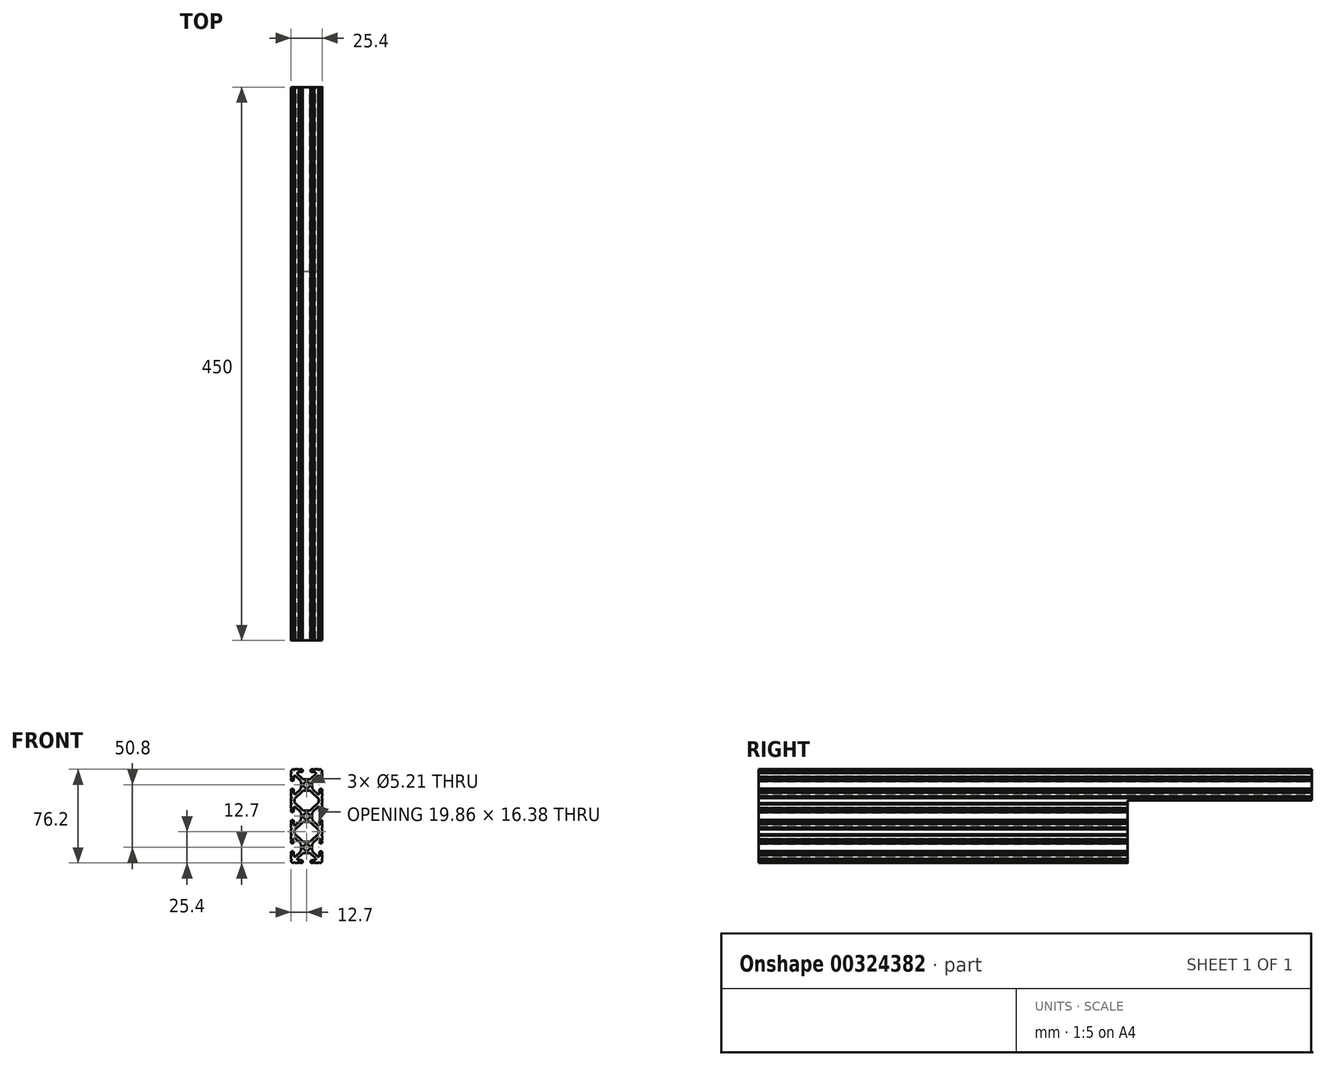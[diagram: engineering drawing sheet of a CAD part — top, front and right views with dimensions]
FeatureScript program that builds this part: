
annotation { "Feature Type Name" : "Feature", "Feature Type Description" : "" }
export const myFeature = defineFeature(function(context is Context, id is Id, definition is map)
    precondition{}
    {
        {
            var Q0;
            Q0=qCreatedBy(makeId("Front.planeOp"),FACE);
            var sketch = newSketch(context, id + "F0", { "sketchPlane" : qUnion([Q0])});
            skArc(sketch, "E0", {"start": v(2.6, 25.4) * mm, "mid": v(0, 28) * mm, "end": v(-2.6, 25.4) * mm});
            skArc(sketch, "E1", {"start": v(-2.6, 25.4) * mm, "mid": v(0, 22.8) * mm, "end": v(2.6, 25.4) * mm});
            skArc(sketch, "E2", {"start": v(-10.57, 38.1) * mm, "mid": v(-10.06, 37.6) * mm, "end": v(-9.55, 38.1) * mm});
            skArc(sketch, "E3", {"start": v(-10.57, 38.1) * mm, "mid": v(-12.08, 37.48) * mm, "end": v(-12.7, 35.97) * mm});
            skArc(sketch, "E4", {"start": v(-12.7, 34.95) * mm, "mid": v(-12.2, 35.46) * mm, "end": v(-12.7, 35.97) * mm});
            skLineSegment(sketch, "E5", {"start": v(-12.7, 34.95) * mm, "end": v(-12.7, 31.72) * mm});
            skArc(sketch, "E6", {"start": v(-12.7, 30.7) * mm, "mid": v(-12.2, 31.22) * mm, "end": v(-12.7, 31.72) * mm});
            skLineSegment(sketch, "E7", {"start": v(-12.7, 30.7) * mm, "end": v(-12.7, 29.7) * mm});
            skArc(sketch, "E8", {"start": v(-12.7, 29.7) * mm, "mid": v(-11.6, 28.6) * mm, "end": v(-10.5, 29.7) * mm});
            skLineSegment(sketch, "E9", {"start": v(-10.5, 29.7) * mm, "end": v(-10.5, 31.87) * mm});
            skArc(sketch, "E10", {"start": v(-8.76, 32.6) * mm, "mid": v(-9.86, 32.81) * mm, "end": v(-10.5, 31.87) * mm});
            skLineSegment(sketch, "E11", {"start": v(-8.76, 32.6) * mm, "end": v(-5.44, 29.28) * mm});
            skArc(sketch, "E12", {"start": v(-4.5, 27.03) * mm, "mid": v(-4.75, 28.25) * mm, "end": v(-5.44, 29.28) * mm});
            skLineSegment(sketch, "E13", {"start": v(-4.5, 27.03) * mm, "end": v(-4.5, 23.77) * mm});
            skArc(sketch, "E14", {"start": v(-5.44, 21.52) * mm, "mid": v(-4.75, 22.55) * mm, "end": v(-4.5, 23.77) * mm});
            skLineSegment(sketch, "E15", {"start": v(-5.44, 21.52) * mm, "end": v(-8.76, 18.2) * mm});
            skArc(sketch, "E16", {"start": v(-10.5, 18.93) * mm, "mid": v(-9.86, 17.99) * mm, "end": v(-8.76, 18.2) * mm});
            skLineSegment(sketch, "E17", {"start": v(-10.5, 18.93) * mm, "end": v(-10.5, 21.1) * mm});
            skArc(sketch, "E18", {"start": v(-10.5, 21.1) * mm, "mid": v(-11.6, 22.2) * mm, "end": v(-12.7, 21.1) * mm});
            skLineSegment(sketch, "E19", {"start": v(-12.7, 21.1) * mm, "end": v(-12.7, 20.1) * mm});
            skArc(sketch, "E20", {"start": v(-12.7, 19.08) * mm, "mid": v(-12.2, 19.58) * mm, "end": v(-12.7, 20.1) * mm});
            skLineSegment(sketch, "E21", {"start": v(-12.7, 19.08) * mm, "end": v(-12.7, 15.85) * mm});
            skArc(sketch, "E22", {"start": v(-12.7, 14.83) * mm, "mid": v(-12.2, 15.34) * mm, "end": v(-12.7, 15.85) * mm});
            skLineSegment(sketch, "E23", {"start": v(-12.7, 14.83) * mm, "end": v(-12.7, 10.57) * mm});
            skArc(sketch, "E24", {"start": v(-12.7, 9.55) * mm, "mid": v(-12.2, 10.06) * mm, "end": v(-12.7, 10.57) * mm});
            skLineSegment(sketch, "E25", {"start": v(-12.7, 9.55) * mm, "end": v(-12.7, 6.32) * mm});
            skArc(sketch, "E26", {"start": v(-12.7, 5.3) * mm, "mid": v(-12.2, 5.82) * mm, "end": v(-12.7, 6.32) * mm});
            skLineSegment(sketch, "E27", {"start": v(-12.7, 5.3) * mm, "end": v(-12.7, 4.3) * mm});
            skArc(sketch, "E28", {"start": v(-12.7, 4.3) * mm, "mid": v(-11.6, 3.2) * mm, "end": v(-10.5, 4.3) * mm});
            skLineSegment(sketch, "E29", {"start": v(-10.5, 4.3) * mm, "end": v(-10.5, 6.47) * mm});
            skArc(sketch, "E30", {"start": v(-8.76, 7.2) * mm, "mid": v(-9.86, 7.41) * mm, "end": v(-10.5, 6.47) * mm});
            skLineSegment(sketch, "E31", {"start": v(-8.76, 7.2) * mm, "end": v(-5.44, 3.88) * mm});
            skArc(sketch, "E32", {"start": v(-4.5, 1.63) * mm, "mid": v(-4.75, 2.85) * mm, "end": v(-5.44, 3.88) * mm});
            skLineSegment(sketch, "E33", {"start": v(-4.5, 1.63) * mm, "end": v(-4.5, -1.63) * mm});
            skArc(sketch, "E34", {"start": v(-5.44, -3.88) * mm, "mid": v(-4.75, -2.85) * mm, "end": v(-4.5, -1.63) * mm});
            skLineSegment(sketch, "E35", {"start": v(-5.44, -3.88) * mm, "end": v(-8.76, -7.2) * mm});
            skArc(sketch, "E36", {"start": v(-10.5, -6.47) * mm, "mid": v(-9.86, -7.41) * mm, "end": v(-8.76, -7.2) * mm});
            skLineSegment(sketch, "E37", {"start": v(-10.5, -6.47) * mm, "end": v(-10.5, -4.3) * mm});
            skArc(sketch, "E38", {"start": v(-10.5, -4.3) * mm, "mid": v(-11.6, -3.2) * mm, "end": v(-12.7, -4.3) * mm});
            skLineSegment(sketch, "E39", {"start": v(-12.7, -4.3) * mm, "end": v(-12.7, -5.3) * mm});
            skArc(sketch, "E40", {"start": v(-12.7, -6.32) * mm, "mid": v(-12.2, -5.82) * mm, "end": v(-12.7, -5.3) * mm});
            skLineSegment(sketch, "E41", {"start": v(-12.7, -6.32) * mm, "end": v(-12.7, -9.55) * mm});
            skArc(sketch, "E42", {"start": v(-12.7, -10.57) * mm, "mid": v(-12.2, -10.06) * mm, "end": v(-12.7, -9.55) * mm});
            skLineSegment(sketch, "E43", {"start": v(-12.7, -10.57) * mm, "end": v(-12.7, -14.83) * mm});
            skArc(sketch, "E44", {"start": v(-12.7, -15.85) * mm, "mid": v(-12.2, -15.34) * mm, "end": v(-12.7, -14.83) * mm});
            skLineSegment(sketch, "E45", {"start": v(-12.7, -15.85) * mm, "end": v(-12.7, -19.08) * mm});
            skArc(sketch, "E46", {"start": v(-12.7, -20.1) * mm, "mid": v(-12.2, -19.58) * mm, "end": v(-12.7, -19.08) * mm});
            skLineSegment(sketch, "E47", {"start": v(-12.7, -20.1) * mm, "end": v(-12.7, -21.1) * mm});
            skArc(sketch, "E48", {"start": v(-12.7, -21.1) * mm, "mid": v(-11.6, -22.2) * mm, "end": v(-10.5, -21.1) * mm});
            skLineSegment(sketch, "E49", {"start": v(-10.5, -21.1) * mm, "end": v(-10.5, -18.93) * mm});
            skArc(sketch, "E50", {"start": v(-8.76, -18.2) * mm, "mid": v(-9.86, -17.99) * mm, "end": v(-10.5, -18.93) * mm});
            skLineSegment(sketch, "E51", {"start": v(-8.76, -18.2) * mm, "end": v(-5.44, -21.52) * mm});
            skArc(sketch, "E52", {"start": v(-4.5, -23.77) * mm, "mid": v(-4.75, -22.55) * mm, "end": v(-5.44, -21.52) * mm});
            skLineSegment(sketch, "E53", {"start": v(-4.5, -23.77) * mm, "end": v(-4.5, -27.03) * mm});
            skArc(sketch, "E54", {"start": v(-5.44, -29.28) * mm, "mid": v(-4.75, -28.25) * mm, "end": v(-4.5, -27.03) * mm});
            skLineSegment(sketch, "E55", {"start": v(-5.44, -29.28) * mm, "end": v(-8.76, -32.6) * mm});
            skArc(sketch, "E56", {"start": v(-10.5, -31.87) * mm, "mid": v(-9.86, -32.81) * mm, "end": v(-8.76, -32.6) * mm});
            skLineSegment(sketch, "E57", {"start": v(-10.5, -31.87) * mm, "end": v(-10.5, -29.7) * mm});
            skArc(sketch, "E58", {"start": v(-10.5, -29.7) * mm, "mid": v(-11.6, -28.6) * mm, "end": v(-12.7, -29.7) * mm});
            skLineSegment(sketch, "E59", {"start": v(-12.7, -29.7) * mm, "end": v(-12.7, -30.7) * mm});
            skArc(sketch, "E60", {"start": v(-12.7, -31.72) * mm, "mid": v(-12.2, -31.22) * mm, "end": v(-12.7, -30.7) * mm});
            skLineSegment(sketch, "E61", {"start": v(-12.7, -31.72) * mm, "end": v(-12.7, -34.95) * mm});
            skArc(sketch, "E62", {"start": v(-12.7, -35.97) * mm, "mid": v(-12.2, -35.46) * mm, "end": v(-12.7, -34.95) * mm});
            skArc(sketch, "E63", {"start": v(-12.7, -35.97) * mm, "mid": v(-12.08, -37.48) * mm, "end": v(-10.57, -38.1) * mm});
            skArc(sketch, "E64", {"start": v(-9.55, -38.1) * mm, "mid": v(-10.06, -37.6) * mm, "end": v(-10.57, -38.1) * mm});
            skLineSegment(sketch, "E65", {"start": v(-9.55, -38.1) * mm, "end": v(-6.32, -38.1) * mm});
            skArc(sketch, "E66", {"start": v(-5.3, -38.1) * mm, "mid": v(-5.82, -37.6) * mm, "end": v(-6.32, -38.1) * mm});
            skLineSegment(sketch, "E67", {"start": v(-5.3, -38.1) * mm, "end": v(-4.3, -38.1) * mm});
            skArc(sketch, "E68", {"start": v(-4.3, -38.1) * mm, "mid": v(-3.2, -37) * mm, "end": v(-4.3, -35.9) * mm});
            skLineSegment(sketch, "E69", {"start": v(-4.3, -35.9) * mm, "end": v(-6.47, -35.9) * mm});
            skArc(sketch, "E70", {"start": v(-7.2, -34.16) * mm, "mid": v(-7.41, -35.26) * mm, "end": v(-6.47, -35.9) * mm});
            skLineSegment(sketch, "E71", {"start": v(-7.2, -34.16) * mm, "end": v(-3.88, -30.84) * mm});
            skArc(sketch, "E72", {"start": v(-1.63, -29.9) * mm, "mid": v(-2.85, -30.15) * mm, "end": v(-3.88, -30.84) * mm});
            skLineSegment(sketch, "E73", {"start": v(-1.63, -29.9) * mm, "end": v(1.63, -29.9) * mm});
            skArc(sketch, "E74", {"start": v(3.88, -30.84) * mm, "mid": v(2.85, -30.15) * mm, "end": v(1.63, -29.9) * mm});
            skLineSegment(sketch, "E75", {"start": v(3.88, -30.84) * mm, "end": v(7.2, -34.16) * mm});
            skArc(sketch, "E76", {"start": v(6.47, -35.9) * mm, "mid": v(7.41, -35.26) * mm, "end": v(7.2, -34.16) * mm});
            skLineSegment(sketch, "E77", {"start": v(6.47, -35.9) * mm, "end": v(4.3, -35.9) * mm});
            skArc(sketch, "E78", {"start": v(4.3, -35.9) * mm, "mid": v(3.2, -37) * mm, "end": v(4.3, -38.1) * mm});
            skLineSegment(sketch, "E79", {"start": v(4.3, -38.1) * mm, "end": v(5.3, -38.1) * mm});
            skArc(sketch, "E80", {"start": v(6.32, -38.1) * mm, "mid": v(5.82, -37.6) * mm, "end": v(5.3, -38.1) * mm});
            skLineSegment(sketch, "E81", {"start": v(6.32, -38.1) * mm, "end": v(9.55, -38.1) * mm});
            skArc(sketch, "E82", {"start": v(10.57, -38.1) * mm, "mid": v(10.06, -37.6) * mm, "end": v(9.55, -38.1) * mm});
            skArc(sketch, "E83", {"start": v(10.57, -38.1) * mm, "mid": v(12.08, -37.48) * mm, "end": v(12.7, -35.97) * mm});
            skArc(sketch, "E84", {"start": v(12.7, -34.95) * mm, "mid": v(12.2, -35.46) * mm, "end": v(12.7, -35.97) * mm});
            skLineSegment(sketch, "E85", {"start": v(12.7, -34.95) * mm, "end": v(12.7, -31.72) * mm});
            skArc(sketch, "E86", {"start": v(12.7, -30.7) * mm, "mid": v(12.2, -31.22) * mm, "end": v(12.7, -31.72) * mm});
            skLineSegment(sketch, "E87", {"start": v(12.7, -30.7) * mm, "end": v(12.7, -29.7) * mm});
            skArc(sketch, "E88", {"start": v(12.7, -29.7) * mm, "mid": v(11.6, -28.6) * mm, "end": v(10.5, -29.7) * mm});
            skLineSegment(sketch, "E89", {"start": v(10.5, -29.7) * mm, "end": v(10.5, -31.87) * mm});
            skArc(sketch, "E90", {"start": v(8.76, -32.6) * mm, "mid": v(9.86, -32.81) * mm, "end": v(10.5, -31.87) * mm});
            skLineSegment(sketch, "E91", {"start": v(8.76, -32.6) * mm, "end": v(5.44, -29.28) * mm});
            skArc(sketch, "E92", {"start": v(4.5, -27.03) * mm, "mid": v(4.75, -28.25) * mm, "end": v(5.44, -29.28) * mm});
            skLineSegment(sketch, "E93", {"start": v(4.5, -27.03) * mm, "end": v(4.5, -23.77) * mm});
            skArc(sketch, "E94", {"start": v(5.44, -21.52) * mm, "mid": v(4.75, -22.55) * mm, "end": v(4.5, -23.77) * mm});
            skLineSegment(sketch, "E95", {"start": v(5.44, -21.52) * mm, "end": v(8.76, -18.2) * mm});
            skArc(sketch, "E96", {"start": v(10.5, -18.93) * mm, "mid": v(9.86, -17.99) * mm, "end": v(8.76, -18.2) * mm});
            skLineSegment(sketch, "E97", {"start": v(10.5, -18.93) * mm, "end": v(10.5, -21.1) * mm});
            skArc(sketch, "E98", {"start": v(10.5, -21.1) * mm, "mid": v(11.6, -22.2) * mm, "end": v(12.7, -21.1) * mm});
            skLineSegment(sketch, "E99", {"start": v(12.7, -21.1) * mm, "end": v(12.7, -20.1) * mm});
            skArc(sketch, "E100", {"start": v(12.7, -19.08) * mm, "mid": v(12.2, -19.58) * mm, "end": v(12.7, -20.1) * mm});
            skLineSegment(sketch, "E101", {"start": v(12.7, -19.08) * mm, "end": v(12.7, -15.85) * mm});
            skArc(sketch, "E102", {"start": v(12.7, -14.83) * mm, "mid": v(12.2, -15.34) * mm, "end": v(12.7, -15.85) * mm});
            skLineSegment(sketch, "E103", {"start": v(12.7, -14.83) * mm, "end": v(12.7, -10.57) * mm});
            skArc(sketch, "E104", {"start": v(12.7, -9.55) * mm, "mid": v(12.2, -10.06) * mm, "end": v(12.7, -10.57) * mm});
            skLineSegment(sketch, "E105", {"start": v(12.7, -9.55) * mm, "end": v(12.7, -6.32) * mm});
            skArc(sketch, "E106", {"start": v(12.7, -5.3) * mm, "mid": v(12.2, -5.82) * mm, "end": v(12.7, -6.32) * mm});
            skLineSegment(sketch, "E107", {"start": v(12.7, -5.3) * mm, "end": v(12.7, -4.3) * mm});
            skArc(sketch, "E108", {"start": v(12.7, -4.3) * mm, "mid": v(11.6, -3.2) * mm, "end": v(10.5, -4.3) * mm});
            skLineSegment(sketch, "E109", {"start": v(10.5, -4.3) * mm, "end": v(10.5, -6.47) * mm});
            skArc(sketch, "E110", {"start": v(8.76, -7.2) * mm, "mid": v(9.86, -7.41) * mm, "end": v(10.5, -6.47) * mm});
            skLineSegment(sketch, "E111", {"start": v(8.76, -7.2) * mm, "end": v(5.44, -3.88) * mm});
            skArc(sketch, "E112", {"start": v(4.5, -1.63) * mm, "mid": v(4.75, -2.85) * mm, "end": v(5.44, -3.88) * mm});
            skLineSegment(sketch, "E113", {"start": v(4.5, -1.63) * mm, "end": v(4.5, 1.63) * mm});
            skArc(sketch, "E114", {"start": v(5.44, 3.88) * mm, "mid": v(4.75, 2.85) * mm, "end": v(4.5, 1.63) * mm});
            skLineSegment(sketch, "E115", {"start": v(5.44, 3.88) * mm, "end": v(8.76, 7.2) * mm});
            skArc(sketch, "E116", {"start": v(10.5, 6.47) * mm, "mid": v(9.86, 7.41) * mm, "end": v(8.76, 7.2) * mm});
            skLineSegment(sketch, "E117", {"start": v(10.5, 6.47) * mm, "end": v(10.5, 4.3) * mm});
            skArc(sketch, "E118", {"start": v(10.5, 4.3) * mm, "mid": v(11.6, 3.2) * mm, "end": v(12.7, 4.3) * mm});
            skLineSegment(sketch, "E119", {"start": v(12.7, 4.3) * mm, "end": v(12.7, 5.3) * mm});
            skArc(sketch, "E120", {"start": v(12.7, 6.32) * mm, "mid": v(12.2, 5.82) * mm, "end": v(12.7, 5.3) * mm});
            skLineSegment(sketch, "E121", {"start": v(12.7, 6.32) * mm, "end": v(12.7, 9.55) * mm});
            skArc(sketch, "E122", {"start": v(12.7, 10.57) * mm, "mid": v(12.2, 10.06) * mm, "end": v(12.7, 9.55) * mm});
            skLineSegment(sketch, "E123", {"start": v(12.7, 10.57) * mm, "end": v(12.7, 14.83) * mm});
            skArc(sketch, "E124", {"start": v(12.7, 15.85) * mm, "mid": v(12.2, 15.34) * mm, "end": v(12.7, 14.83) * mm});
            skLineSegment(sketch, "E125", {"start": v(12.7, 15.85) * mm, "end": v(12.7, 19.08) * mm});
            skArc(sketch, "E126", {"start": v(12.7, 20.1) * mm, "mid": v(12.2, 19.58) * mm, "end": v(12.7, 19.08) * mm});
            skLineSegment(sketch, "E127", {"start": v(12.7, 20.1) * mm, "end": v(12.7, 21.1) * mm});
            skArc(sketch, "E128", {"start": v(12.7, 21.1) * mm, "mid": v(11.6, 22.2) * mm, "end": v(10.5, 21.1) * mm});
            skLineSegment(sketch, "E129", {"start": v(10.5, 21.1) * mm, "end": v(10.5, 18.93) * mm});
            skArc(sketch, "E130", {"start": v(8.76, 18.2) * mm, "mid": v(9.86, 17.99) * mm, "end": v(10.5, 18.93) * mm});
            skLineSegment(sketch, "E131", {"start": v(8.76, 18.2) * mm, "end": v(5.44, 21.52) * mm});
            skArc(sketch, "E132", {"start": v(4.5, 23.77) * mm, "mid": v(4.75, 22.55) * mm, "end": v(5.44, 21.52) * mm});
            skLineSegment(sketch, "E133", {"start": v(4.5, 23.77) * mm, "end": v(4.5, 27.03) * mm});
            skArc(sketch, "E134", {"start": v(5.44, 29.28) * mm, "mid": v(4.75, 28.25) * mm, "end": v(4.5, 27.03) * mm});
            skLineSegment(sketch, "E135", {"start": v(5.44, 29.28) * mm, "end": v(8.76, 32.6) * mm});
            skArc(sketch, "E136", {"start": v(10.5, 31.87) * mm, "mid": v(9.86, 32.81) * mm, "end": v(8.76, 32.6) * mm});
            skLineSegment(sketch, "E137", {"start": v(10.5, 31.87) * mm, "end": v(10.5, 29.7) * mm});
            skArc(sketch, "E138", {"start": v(10.5, 29.7) * mm, "mid": v(11.6, 28.6) * mm, "end": v(12.7, 29.7) * mm});
            skLineSegment(sketch, "E139", {"start": v(12.7, 29.7) * mm, "end": v(12.7, 30.7) * mm});
            skArc(sketch, "E140", {"start": v(12.7, 31.72) * mm, "mid": v(12.2, 31.22) * mm, "end": v(12.7, 30.7) * mm});
            skLineSegment(sketch, "E141", {"start": v(12.7, 31.72) * mm, "end": v(12.7, 34.95) * mm});
            skArc(sketch, "E142", {"start": v(12.7, 35.97) * mm, "mid": v(12.2, 35.46) * mm, "end": v(12.7, 34.95) * mm});
            skArc(sketch, "E143", {"start": v(12.7, 35.97) * mm, "mid": v(12.08, 37.48) * mm, "end": v(10.57, 38.1) * mm});
            skArc(sketch, "E144", {"start": v(9.55, 38.1) * mm, "mid": v(10.06, 37.6) * mm, "end": v(10.57, 38.1) * mm});
            skLineSegment(sketch, "E145", {"start": v(9.55, 38.1) * mm, "end": v(6.32, 38.1) * mm});
            skArc(sketch, "E146", {"start": v(5.3, 38.1) * mm, "mid": v(5.82, 37.6) * mm, "end": v(6.32, 38.1) * mm});
            skLineSegment(sketch, "E147", {"start": v(5.3, 38.1) * mm, "end": v(4.3, 38.1) * mm});
            skArc(sketch, "E148", {"start": v(4.3, 38.1) * mm, "mid": v(3.2, 37) * mm, "end": v(4.3, 35.9) * mm});
            skLineSegment(sketch, "E149", {"start": v(4.3, 35.9) * mm, "end": v(6.47, 35.9) * mm});
            skArc(sketch, "E150", {"start": v(7.2, 34.16) * mm, "mid": v(7.41, 35.26) * mm, "end": v(6.47, 35.9) * mm});
            skLineSegment(sketch, "E151", {"start": v(7.2, 34.16) * mm, "end": v(3.88, 30.84) * mm});
            skArc(sketch, "E152", {"start": v(1.63, 29.9) * mm, "mid": v(2.85, 30.15) * mm, "end": v(3.88, 30.84) * mm});
            skLineSegment(sketch, "E153", {"start": v(1.63, 29.9) * mm, "end": v(-1.63, 29.9) * mm});
            skArc(sketch, "E154", {"start": v(-3.88, 30.84) * mm, "mid": v(-2.85, 30.15) * mm, "end": v(-1.63, 29.9) * mm});
            skLineSegment(sketch, "E155", {"start": v(-3.88, 30.84) * mm, "end": v(-7.2, 34.16) * mm});
            skArc(sketch, "E156", {"start": v(-6.47, 35.9) * mm, "mid": v(-7.41, 35.26) * mm, "end": v(-7.2, 34.16) * mm});
            skLineSegment(sketch, "E157", {"start": v(-6.47, 35.9) * mm, "end": v(-4.3, 35.9) * mm});
            skArc(sketch, "E158", {"start": v(-4.3, 35.9) * mm, "mid": v(-3.2, 37) * mm, "end": v(-4.3, 38.1) * mm});
            skLineSegment(sketch, "E159", {"start": v(-4.3, 38.1) * mm, "end": v(-5.3, 38.1) * mm});
            skArc(sketch, "E160", {"start": v(-6.32, 38.1) * mm, "mid": v(-5.82, 37.6) * mm, "end": v(-5.3, 38.1) * mm});
            skLineSegment(sketch, "E161", {"start": v(-6.32, 38.1) * mm, "end": v(-9.55, 38.1) * mm});
            skArc(sketch, "E162", {"start": v(2.6, 0) * mm, "mid": v(0, 2.6) * mm, "end": v(-2.6, 0) * mm});
            skArc(sketch, "E163", {"start": v(-2.6, 0) * mm, "mid": v(0, -2.6) * mm, "end": v(2.6, 0) * mm});
            skArc(sketch, "E164", {"start": v(2.6, -25.4) * mm, "mid": v(0, -22.8) * mm, "end": v(-2.6, -25.4) * mm});
            skArc(sketch, "E165", {"start": v(-2.6, -25.4) * mm, "mid": v(0, -28) * mm, "end": v(2.6, -25.4) * mm});
            skLineSegment(sketch, "E166", {"start": v(-3.88, -5.44) * mm, "end": v(-9.47, -11.03) * mm});
            skArc(sketch, "E167", {"start": v(-1.63, -4.5) * mm, "mid": v(-2.85, -4.75) * mm, "end": v(-3.88, -5.44) * mm});
            skLineSegment(sketch, "E168", {"start": v(1.63, -4.5) * mm, "end": v(-1.63, -4.5) * mm});
            skArc(sketch, "E169", {"start": v(3.88, -5.44) * mm, "mid": v(2.85, -4.75) * mm, "end": v(1.63, -4.5) * mm});
            skLineSegment(sketch, "E170", {"start": v(9.47, -11.03) * mm, "end": v(3.88, -5.44) * mm});
            skArc(sketch, "E171", {"start": v(9.93, -12.15) * mm, "mid": v(9.81, -11.54) * mm, "end": v(9.47, -11.03) * mm});
            skLineSegment(sketch, "E172", {"start": v(9.93, -13.25) * mm, "end": v(9.93, -12.15) * mm});
            skArc(sketch, "E173", {"start": v(9.47, -14.37) * mm, "mid": v(9.81, -13.86) * mm, "end": v(9.93, -13.25) * mm});
            skLineSegment(sketch, "E174", {"start": v(3.88, -19.96) * mm, "end": v(9.47, -14.37) * mm});
            skArc(sketch, "E175", {"start": v(1.63, -20.9) * mm, "mid": v(2.85, -20.65) * mm, "end": v(3.88, -19.96) * mm});
            skLineSegment(sketch, "E176", {"start": v(-1.63, -20.9) * mm, "end": v(1.63, -20.9) * mm});
            skArc(sketch, "E177", {"start": v(-3.88, -19.96) * mm, "mid": v(-2.85, -20.65) * mm, "end": v(-1.63, -20.9) * mm});
            skLineSegment(sketch, "E178", {"start": v(-9.47, -14.37) * mm, "end": v(-3.88, -19.96) * mm});
            skArc(sketch, "E179", {"start": v(-9.93, -13.25) * mm, "mid": v(-9.81, -13.86) * mm, "end": v(-9.47, -14.37) * mm});
            skLineSegment(sketch, "E180", {"start": v(-9.93, -12.15) * mm, "end": v(-9.93, -13.25) * mm});
            skArc(sketch, "E181", {"start": v(-9.47, -11.03) * mm, "mid": v(-9.81, -11.54) * mm, "end": v(-9.93, -12.15) * mm});
            skLineSegment(sketch, "E182", {"start": v(-3.88, 19.96) * mm, "end": v(-9.47, 14.37) * mm});
            skArc(sketch, "E183", {"start": v(-1.63, 20.9) * mm, "mid": v(-2.85, 20.65) * mm, "end": v(-3.88, 19.96) * mm});
            skLineSegment(sketch, "E184", {"start": v(1.63, 20.9) * mm, "end": v(-1.63, 20.9) * mm});
            skArc(sketch, "E185", {"start": v(3.88, 19.96) * mm, "mid": v(2.85, 20.65) * mm, "end": v(1.63, 20.9) * mm});
            skLineSegment(sketch, "E186", {"start": v(9.47, 14.37) * mm, "end": v(3.88, 19.96) * mm});
            skArc(sketch, "E187", {"start": v(9.93, 13.25) * mm, "mid": v(9.81, 13.86) * mm, "end": v(9.47, 14.37) * mm});
            skLineSegment(sketch, "E188", {"start": v(9.93, 12.15) * mm, "end": v(9.93, 13.25) * mm});
            skArc(sketch, "E189", {"start": v(9.47, 11.03) * mm, "mid": v(9.81, 11.54) * mm, "end": v(9.93, 12.15) * mm});
            skLineSegment(sketch, "E190", {"start": v(3.88, 5.44) * mm, "end": v(9.47, 11.03) * mm});
            skArc(sketch, "E191", {"start": v(1.63, 4.5) * mm, "mid": v(2.85, 4.75) * mm, "end": v(3.88, 5.44) * mm});
            skLineSegment(sketch, "E192", {"start": v(-1.63, 4.5) * mm, "end": v(1.63, 4.5) * mm});
            skArc(sketch, "E193", {"start": v(-3.88, 5.44) * mm, "mid": v(-2.85, 4.75) * mm, "end": v(-1.63, 4.5) * mm});
            skLineSegment(sketch, "E194", {"start": v(-9.47, 11.03) * mm, "end": v(-3.88, 5.44) * mm});
            skArc(sketch, "E195", {"start": v(-9.93, 12.15) * mm, "mid": v(-9.81, 11.54) * mm, "end": v(-9.47, 11.03) * mm});
            skLineSegment(sketch, "E196", {"start": v(-9.93, 13.25) * mm, "end": v(-9.93, 12.15) * mm});
            skArc(sketch, "E197", {"start": v(-9.47, 14.37) * mm, "mid": v(-9.81, 13.86) * mm, "end": v(-9.93, 13.25) * mm});
            skSolve(sketch);
        }
        {
            var Q0;
            Q0=makeQuery(id+"F0.imprint","IMPRINT",FACE,{"disambiguationData":[TD([[makeQuery(id+"F0.imprint","IMPRINT",EDGE,{"derivedFrom":sQuery(id+"F0.wireOp",EDGE,"E0")}),-1.0]])]});
            extrude(context, id + "F1", {"entities" : qUnion([Q0]), "depth" : 450 * mm});
        }
        {
            var Q0;
            Q0=makeQuery(id+"F1.opExtrude","CAP_FACE",FACE,{"disambiguationData":[OSD([sQuery(id+"F0.wireOp",EDGE,"E0"),sQuery(id+"F0.wireOp",EDGE,"E1"),sQuery(id+"F0.wireOp",EDGE,"E2"),sQuery(id+"F0.wireOp",EDGE,"E3"),sQuery(id+"F0.wireOp",EDGE,"E4"),sQuery(id+"F0.wireOp",EDGE,"E5"),sQuery(id+"F0.wireOp",EDGE,"E6"),sQuery(id+"F0.wireOp",EDGE,"E7"),sQuery(id+"F0.wireOp",EDGE,"E8"),sQuery(id+"F0.wireOp",EDGE,"E9"),sQuery(id+"F0.wireOp",EDGE,"E10"),sQuery(id+"F0.wireOp",EDGE,"E11"),sQuery(id+"F0.wireOp",EDGE,"E12"),sQuery(id+"F0.wireOp",EDGE,"E13"),sQuery(id+"F0.wireOp",EDGE,"E14"),sQuery(id+"F0.wireOp",EDGE,"E15"),sQuery(id+"F0.wireOp",EDGE,"E16"),sQuery(id+"F0.wireOp",EDGE,"E17"),sQuery(id+"F0.wireOp",EDGE,"E18"),sQuery(id+"F0.wireOp",EDGE,"E19"),sQuery(id+"F0.wireOp",EDGE,"E20"),sQuery(id+"F0.wireOp",EDGE,"E21"),sQuery(id+"F0.wireOp",EDGE,"E22"),sQuery(id+"F0.wireOp",EDGE,"E23"),sQuery(id+"F0.wireOp",EDGE,"E24"),sQuery(id+"F0.wireOp",EDGE,"E25"),sQuery(id+"F0.wireOp",EDGE,"E26"),sQuery(id+"F0.wireOp",EDGE,"E27"),sQuery(id+"F0.wireOp",EDGE,"E28"),sQuery(id+"F0.wireOp",EDGE,"E29"),sQuery(id+"F0.wireOp",EDGE,"E30"),sQuery(id+"F0.wireOp",EDGE,"E31"),sQuery(id+"F0.wireOp",EDGE,"E32"),sQuery(id+"F0.wireOp",EDGE,"E33"),sQuery(id+"F0.wireOp",EDGE,"E34"),sQuery(id+"F0.wireOp",EDGE,"E35"),sQuery(id+"F0.wireOp",EDGE,"E36"),sQuery(id+"F0.wireOp",EDGE,"E37"),sQuery(id+"F0.wireOp",EDGE,"E38"),sQuery(id+"F0.wireOp",EDGE,"E39"),sQuery(id+"F0.wireOp",EDGE,"E40"),sQuery(id+"F0.wireOp",EDGE,"E41"),sQuery(id+"F0.wireOp",EDGE,"E42"),sQuery(id+"F0.wireOp",EDGE,"E43"),sQuery(id+"F0.wireOp",EDGE,"E44"),sQuery(id+"F0.wireOp",EDGE,"E45"),sQuery(id+"F0.wireOp",EDGE,"E46"),sQuery(id+"F0.wireOp",EDGE,"E47"),sQuery(id+"F0.wireOp",EDGE,"E48"),sQuery(id+"F0.wireOp",EDGE,"E49"),sQuery(id+"F0.wireOp",EDGE,"E50"),sQuery(id+"F0.wireOp",EDGE,"E51"),sQuery(id+"F0.wireOp",EDGE,"E52"),sQuery(id+"F0.wireOp",EDGE,"E53"),sQuery(id+"F0.wireOp",EDGE,"E54"),sQuery(id+"F0.wireOp",EDGE,"E55"),sQuery(id+"F0.wireOp",EDGE,"E56"),sQuery(id+"F0.wireOp",EDGE,"E57"),sQuery(id+"F0.wireOp",EDGE,"E58"),sQuery(id+"F0.wireOp",EDGE,"E59"),sQuery(id+"F0.wireOp",EDGE,"E60"),sQuery(id+"F0.wireOp",EDGE,"E61"),sQuery(id+"F0.wireOp",EDGE,"E62"),sQuery(id+"F0.wireOp",EDGE,"E63"),sQuery(id+"F0.wireOp",EDGE,"E64"),sQuery(id+"F0.wireOp",EDGE,"E65"),sQuery(id+"F0.wireOp",EDGE,"E66"),sQuery(id+"F0.wireOp",EDGE,"E67"),sQuery(id+"F0.wireOp",EDGE,"E68"),sQuery(id+"F0.wireOp",EDGE,"E69"),sQuery(id+"F0.wireOp",EDGE,"E70"),sQuery(id+"F0.wireOp",EDGE,"E71"),sQuery(id+"F0.wireOp",EDGE,"E72"),sQuery(id+"F0.wireOp",EDGE,"E73"),sQuery(id+"F0.wireOp",EDGE,"E74"),sQuery(id+"F0.wireOp",EDGE,"E75"),sQuery(id+"F0.wireOp",EDGE,"E76"),sQuery(id+"F0.wireOp",EDGE,"E77"),sQuery(id+"F0.wireOp",EDGE,"E78"),sQuery(id+"F0.wireOp",EDGE,"E79"),sQuery(id+"F0.wireOp",EDGE,"E80"),sQuery(id+"F0.wireOp",EDGE,"E81"),sQuery(id+"F0.wireOp",EDGE,"E82"),sQuery(id+"F0.wireOp",EDGE,"E83"),sQuery(id+"F0.wireOp",EDGE,"E84"),sQuery(id+"F0.wireOp",EDGE,"E85"),sQuery(id+"F0.wireOp",EDGE,"E86"),sQuery(id+"F0.wireOp",EDGE,"E87"),sQuery(id+"F0.wireOp",EDGE,"E88"),sQuery(id+"F0.wireOp",EDGE,"E89"),sQuery(id+"F0.wireOp",EDGE,"E90"),sQuery(id+"F0.wireOp",EDGE,"E91"),sQuery(id+"F0.wireOp",EDGE,"E92"),sQuery(id+"F0.wireOp",EDGE,"E93"),sQuery(id+"F0.wireOp",EDGE,"E94"),sQuery(id+"F0.wireOp",EDGE,"E95"),sQuery(id+"F0.wireOp",EDGE,"E96"),sQuery(id+"F0.wireOp",EDGE,"E97"),sQuery(id+"F0.wireOp",EDGE,"E98"),sQuery(id+"F0.wireOp",EDGE,"E99"),sQuery(id+"F0.wireOp",EDGE,"E100"),sQuery(id+"F0.wireOp",EDGE,"E101"),sQuery(id+"F0.wireOp",EDGE,"E102"),sQuery(id+"F0.wireOp",EDGE,"E103"),sQuery(id+"F0.wireOp",EDGE,"E104"),sQuery(id+"F0.wireOp",EDGE,"E105"),sQuery(id+"F0.wireOp",EDGE,"E106"),sQuery(id+"F0.wireOp",EDGE,"E107"),sQuery(id+"F0.wireOp",EDGE,"E108"),sQuery(id+"F0.wireOp",EDGE,"E109"),sQuery(id+"F0.wireOp",EDGE,"E110"),sQuery(id+"F0.wireOp",EDGE,"E111"),sQuery(id+"F0.wireOp",EDGE,"E112"),sQuery(id+"F0.wireOp",EDGE,"E113"),sQuery(id+"F0.wireOp",EDGE,"E114"),sQuery(id+"F0.wireOp",EDGE,"E115"),sQuery(id+"F0.wireOp",EDGE,"E116"),sQuery(id+"F0.wireOp",EDGE,"E117"),sQuery(id+"F0.wireOp",EDGE,"E118"),sQuery(id+"F0.wireOp",EDGE,"E119"),sQuery(id+"F0.wireOp",EDGE,"E120"),sQuery(id+"F0.wireOp",EDGE,"E121"),sQuery(id+"F0.wireOp",EDGE,"E122"),sQuery(id+"F0.wireOp",EDGE,"E123"),sQuery(id+"F0.wireOp",EDGE,"E124"),sQuery(id+"F0.wireOp",EDGE,"E125"),sQuery(id+"F0.wireOp",EDGE,"E126"),sQuery(id+"F0.wireOp",EDGE,"E127"),sQuery(id+"F0.wireOp",EDGE,"E128"),sQuery(id+"F0.wireOp",EDGE,"E129"),sQuery(id+"F0.wireOp",EDGE,"E130"),sQuery(id+"F0.wireOp",EDGE,"E131"),sQuery(id+"F0.wireOp",EDGE,"E132"),sQuery(id+"F0.wireOp",EDGE,"E133"),sQuery(id+"F0.wireOp",EDGE,"E134"),sQuery(id+"F0.wireOp",EDGE,"E135"),sQuery(id+"F0.wireOp",EDGE,"E136"),sQuery(id+"F0.wireOp",EDGE,"E137"),sQuery(id+"F0.wireOp",EDGE,"E138"),sQuery(id+"F0.wireOp",EDGE,"E139"),sQuery(id+"F0.wireOp",EDGE,"E140"),sQuery(id+"F0.wireOp",EDGE,"E141"),sQuery(id+"F0.wireOp",EDGE,"E142"),sQuery(id+"F0.wireOp",EDGE,"E143"),sQuery(id+"F0.wireOp",EDGE,"E144"),sQuery(id+"F0.wireOp",EDGE,"E145"),sQuery(id+"F0.wireOp",EDGE,"E146"),sQuery(id+"F0.wireOp",EDGE,"E147"),sQuery(id+"F0.wireOp",EDGE,"E148"),sQuery(id+"F0.wireOp",EDGE,"E149"),sQuery(id+"F0.wireOp",EDGE,"E150"),sQuery(id+"F0.wireOp",EDGE,"E151"),sQuery(id+"F0.wireOp",EDGE,"E152"),sQuery(id+"F0.wireOp",EDGE,"E153"),sQuery(id+"F0.wireOp",EDGE,"E154"),sQuery(id+"F0.wireOp",EDGE,"E155"),sQuery(id+"F0.wireOp",EDGE,"E156"),sQuery(id+"F0.wireOp",EDGE,"E157"),sQuery(id+"F0.wireOp",EDGE,"E158"),sQuery(id+"F0.wireOp",EDGE,"E159"),sQuery(id+"F0.wireOp",EDGE,"E160"),sQuery(id+"F0.wireOp",EDGE,"E161"),sQuery(id+"F0.wireOp",EDGE,"E162"),sQuery(id+"F0.wireOp",EDGE,"E163"),sQuery(id+"F0.wireOp",EDGE,"E164"),sQuery(id+"F0.wireOp",EDGE,"E165"),sQuery(id+"F0.wireOp",EDGE,"E166"),sQuery(id+"F0.wireOp",EDGE,"E167"),sQuery(id+"F0.wireOp",EDGE,"E168"),sQuery(id+"F0.wireOp",EDGE,"E169"),sQuery(id+"F0.wireOp",EDGE,"E170"),sQuery(id+"F0.wireOp",EDGE,"E171"),sQuery(id+"F0.wireOp",EDGE,"E172"),sQuery(id+"F0.wireOp",EDGE,"E173"),sQuery(id+"F0.wireOp",EDGE,"E174"),sQuery(id+"F0.wireOp",EDGE,"E175"),sQuery(id+"F0.wireOp",EDGE,"E176"),sQuery(id+"F0.wireOp",EDGE,"E177"),sQuery(id+"F0.wireOp",EDGE,"E178"),sQuery(id+"F0.wireOp",EDGE,"E179"),sQuery(id+"F0.wireOp",EDGE,"E180"),sQuery(id+"F0.wireOp",EDGE,"E181"),sQuery(id+"F0.wireOp",EDGE,"E182"),sQuery(id+"F0.wireOp",EDGE,"E183"),sQuery(id+"F0.wireOp",EDGE,"E184"),sQuery(id+"F0.wireOp",EDGE,"E185"),sQuery(id+"F0.wireOp",EDGE,"E186"),sQuery(id+"F0.wireOp",EDGE,"E187"),sQuery(id+"F0.wireOp",EDGE,"E188"),sQuery(id+"F0.wireOp",EDGE,"E189"),sQuery(id+"F0.wireOp",EDGE,"E190"),sQuery(id+"F0.wireOp",EDGE,"E191"),sQuery(id+"F0.wireOp",EDGE,"E192"),sQuery(id+"F0.wireOp",EDGE,"E193"),sQuery(id+"F0.wireOp",EDGE,"E194"),sQuery(id+"F0.wireOp",EDGE,"E195"),sQuery(id+"F0.wireOp",EDGE,"E196"),sQuery(id+"F0.wireOp",EDGE,"E197")])],"isStart":true});
            var sketch = newSketch(context, id + "F2", { "sketchPlane" : qUnion([Q0])});
            skLineSegment(sketch, "E198.bottom", {"start": v(-29.04, 12.7) * mm, "end": v(24.16, 12.7) * mm});
            skLineSegment(sketch, "E198.top", {"start": v(-29.04, -43.49) * mm, "end": v(24.16, -43.49) * mm});
            skLineSegment(sketch, "E198.left", {"start": v(-29.04, 12.7) * mm, "end": v(-29.04, -43.49) * mm});
            skLineSegment(sketch, "E198.right", {"start": v(24.16, 12.7) * mm, "end": v(24.16, -43.49) * mm});
            skPoint(sketch, "E199", {"position": v(-12.7, 12.7) * mm});
            skSolve(sketch);
        }
        {
            var Q0;
            Q0 = qSketchRegion(id + "F2", true);
            extrude(context, id + "F3", {"entities" : qUnion([Q0]), "operationType" : NewBodyOperationType.REMOVE, "oppositeDirection" : true, "depth" : 150 * mm});
        }
    });
